# Revit family: LAMP_HANCE SURFACE MEDIUM FLOOD
name_source: partatom
category: Modelos genéricos
revit_build: Autodesk Revit 2015 (Build: 20140606_1530(x64)
units: mm (PartAtom-declared; Revit-internal decimal feet)

## types (16) — shared parameters
CRI = 80
Comentarios de tipo = Availability of tilting between 0º and 90º, rotation between 0º and 355º and change ring color when placed in a project.
Elevación por defecto = 1219 mm
Fabricante = LAMP
Gear = Electronic
Installation instructions = http://www.lamp.es
Insulation class = I
Lamp = LED COB
Last update = 08/08/2018
MacAdam = 3
Manufacturer URL = http://www.lamp.es
Manufacturer country = Spain
Manufacturer name = LAMP
Model explanation = Availability of tilting between 0º and 90º, rotation between 0º and 355º and change ring color when placed in a project.
Power Supply = 220-240V 50-60Hz
Product URL = http://www.lamp.es
Product datasheet = http://www.lamp.es
Protection rating = IP20
Type = COB PHILIPS

## per-type parameters (varying)
- 751LM 3000 BLACK: Altura tija=63 mm  [stored 0.206693 ft]; Anchura tija=23 mm  [stored 0.0754593 ft]; Body height=135 mm  [stored 0.442913 ft]; Descripción=HANCE SUR 1000 WW MFL BK.; Diameter=65 mm  [stored 0.213255 ft]; Efficacy=92 lm/W; Finish=Texturised black; IEE=A+; Initial color=3000 K; Initial intensity=751 lm; LED Lifetime=50.000 L90 B10; Longitud aro=64 mm  [stored 0.209974 ft]; Longitud cuerpo=135 mm  [stored 0.442913 ft]; Luminaire type=Indoor - Spotlight; Material base=LAMP_Aluminio Hance Negro; Material tija=LAMP_Aluminio Hance Negro; Modelo=HS1SF10MF830NBB; Photometric web file=Cuerpo Hance SURFACE MEDIUM FLOOD (tilting) : 751LM 3000 BLACK; Plum=8 W; Power=7 W; Product code=HS1SF10MF830NBB; Profundidad tija=8 mm  [stored 0.0262467 ft]; Radio bse surface=33 mm; Total height=214 mm  [stored 0.7021 ft]; Weight=0.63 kg
- 751LM 3000 WHITE: Altura tija=63 mm  [stored 0.206693 ft]; Anchura tija=23 mm  [stored 0.0754593 ft]; Body height=135 mm  [stored 0.442913 ft]; Descripción=HANCE SUR 1000 WW MFL WH.; Diameter=65 mm  [stored 0.213255 ft]; Efficacy=92 lm/W; Finish=Texturised matt white; IEE=A+; Initial color=3000 K; Initial intensity=751 lm; LED Lifetime=50.000 L90 B10; Longitud aro=64 mm  [stored 0.209974 ft]; Longitud cuerpo=135 mm  [stored 0.442913 ft]; Luminaire type=Indoor - Spotlight; Material base=LAMP_Aluminio Hance Blanco; Material tija=LAMP_Aluminio Hance Blanco; Modelo=HS1SF10MF830NBW; Photometric web file=Cuerpo Hance SURFACE MEDIUM FLOOD (tilting) : 751LM 3000 WHITE; Plum=8 W; Power=7 W; Product code=HS1SF10MF830NBW; Profundidad tija=8 mm  [stored 0.0262467 ft]; Radio bse surface=33 mm; Total height=214 mm  [stored 0.7021 ft]; Weight=0.62 kg
- 794LM 4000 BLACK: Altura tija=63 mm  [stored 0.206693 ft]; Anchura tija=23 mm  [stored 0.0754593 ft]; Body height=135 mm  [stored 0.442913 ft]; Descripción=HANCE SUR 1000 NW MFL BK.; Diameter=65 mm  [stored 0.213255 ft]; Efficacy=97 lm/W; Finish=Texturised black; IEE=A++; Initial color=4000 K; Initial intensity=794 lm; LED Lifetime=50.000 L90 B10; Longitud aro=64 mm  [stored 0.209974 ft]; Longitud cuerpo=135 mm  [stored 0.442913 ft]; Luminaire type=Indoor - Spotlight; Material base=LAMP_Aluminio Hance Negro; Material tija=LAMP_Aluminio Hance Negro; Modelo=HS1SF10MF840NBB; Photometric web file=Cuerpo Hance SURFACE MEDIUM FLOOD (tilting) : 794LM 4000 BLACK; Plum=8 W; Power=7 W; Product code=HS1SF10MF840NBB; Profundidad tija=8 mm  [stored 0.0262467 ft]; Radio bse surface=33 mm; Total height=214 mm  [stored 0.7021 ft]; Weight=0.62 kg
- 794LM 4000 WHITE: Altura tija=63 mm  [stored 0.206693 ft]; Anchura tija=23 mm  [stored 0.0754593 ft]; Body height=135 mm  [stored 0.442913 ft]; Descripción=HANCE SUR 1000 NW MFL WH.; Diameter=65 mm  [stored 0.213255 ft]; Efficacy=97 lm/W; Finish=Texturised matt white; IEE=A++; Initial color=4000 K; Initial intensity=794 lm; LED Lifetime=50.000 L90 B10; Longitud aro=64 mm  [stored 0.209974 ft]; Longitud cuerpo=135 mm  [stored 0.442913 ft]; Luminaire type=Indoor - spotlight; Material base=LAMP_Aluminio Hance Blanco; Material tija=LAMP_Aluminio Hance Blanco; Modelo=HS1SF10MF840NBW; Photometric web file=Cuerpo Hance SURFACE MEDIUM FLOOD (tilting) : 794LM 4000 WHITE; Plum=8 W; Power=7 W; Product code=HS1SF10MF840NBW; Profundidad tija=8 mm  [stored 0.0262467 ft]; Radio bse surface=33 mm; Total height=214 mm  [stored 0.7021 ft]; Weight=0.62 kg
- 1612LM 3000 BLACK: Altura tija=63 mm  [stored 0.206693 ft]; Anchura tija=23 mm  [stored 0.0754593 ft]; Body height=170 mm  [stored 0.557743 ft]; Descripción=HANCE SUR 2000 WW MFL BK.; Diameter=65 mm  [stored 0.213255 ft]; Efficacy=77 lm/W; Finish=Texturised black; IEE=A+; Initial color=3000 K; Initial intensity=1612 lm; LED Lifetime=50.000 L80 B10; Longitud aro=99 mm; Longitud cuerpo=170 mm  [stored 0.557743 ft]; Luminaire type=Indoor - Spotlight; Material base=LAMP_Aluminio Hance Negro; Material tija=LAMP_Aluminio Hance Negro; Modelo=HS1SF20MF830NBB; Photometric web file=Cuerpo Hance SURFACE MEDIUM FLOOD (tilting) : 1612LM 3000 BLACK; Plum=21 W; Power=18 W; Product code=HS1SF20MF830NBB; Profundidad tija=8 mm  [stored 0.0262467 ft]; Radio bse surface=33 mm; Total height=248 mm  [stored 0.813648 ft]; Weight=0.72 kg
- 1612LM 3000 WHITE: Altura tija=63 mm  [stored 0.206693 ft]; Anchura tija=23 mm  [stored 0.0754593 ft]; Body height=170 mm  [stored 0.557743 ft]; Descripción=HANCE SUR 2000 WW MFL WH.; Diameter=65 mm  [stored 0.213255 ft]; Efficacy=77 lm/W; Finish=Texturised matt white; IEE=A+; Initial color=3000 K; Initial intensity=1612 lm; LED Lifetime=50.000 L80 B10; Longitud aro=99 mm; Longitud cuerpo=170 mm  [stored 0.557743 ft]; Luminaire type=Indoor - Spotlight; Material base=LAMP_Aluminio Hance Blanco; Material tija=LAMP_Aluminio Hance Blanco; Modelo=HS1SF20MF830NBW; Photometric web file=Cuerpo Hance SURFACE MEDIUM FLOOD (tilting) : 1612LM 3000 WHITE; Plum=21 W; Power=18 W; Product code=HS1SF20MF830NBW; Profundidad tija=8 mm  [stored 0.0262467 ft]; Radio bse surface=33 mm; Total height=248 mm  [stored 0.813648 ft]; Weight=0.72 kg
- 1703LM 4000 BLACK: Altura tija=63 mm  [stored 0.206693 ft]; Anchura tija=23 mm  [stored 0.0754593 ft]; Body height=170 mm  [stored 0.557743 ft]; Descripción=HANCE SUR 2000 NW MFL BK.; Diameter=65 mm  [stored 0.213255 ft]; Efficacy=81 lm/W; Finish=Texturised black; IEE=A+; Initial color=4000 K; Initial intensity=1703 lm; LED Lifetime=50.000 L80 B10; Longitud aro=99 mm; Longitud cuerpo=170 mm  [stored 0.557743 ft]; Luminaire type=Indoor - Spotlight; Material base=LAMP_Aluminio Hance Negro; Material tija=LAMP_Aluminio Hance Negro; Modelo=HS1SF20MF840NBB; Photometric web file=Cuerpo Hance SURFACE MEDIUM FLOOD (tilting) : 1703LM 4000 BLACK; Plum=21 W; Power=18 W; Product code=HS1SF20MF840NBB; Profundidad tija=8 mm  [stored 0.0262467 ft]; Radio bse surface=33 mm; Total height=248 mm  [stored 0.813648 ft]; Weight=0.72 kg
- 1703LM 4000 WHITE: Altura tija=63 mm  [stored 0.206693 ft]; Anchura tija=23 mm  [stored 0.0754593 ft]; Body height=170 mm  [stored 0.557743 ft]; Descripción=HANCE SUR 2000 NW MFL WH.; Diameter=65 mm  [stored 0.213255 ft]; Efficacy=81 lm/W; Finish=Texturised matt white; IEE=A+; Initial color=4000 K; Initial intensity=1703 lm; LED Lifetime=50.000 L80 B10; Longitud aro=99 mm; Longitud cuerpo=170 mm  [stored 0.557743 ft]; Luminaire type=Indoor - Spotlight; Material base=LAMP_Aluminio Hance Blanco; Material tija=LAMP_Aluminio Hance Blanco; Modelo=HS1SF20MF840NBW; Photometric web file=Cuerpo Hance SURFACE MEDIUM FLOOD (tilting) : 1703LM 4000 WHITE; Plum=21 W; Power=18 W; Product code=HS1SF20MF840NBW; Profundidad tija=8 mm  [stored 0.0262467 ft]; Radio bse surface=33 mm; Total height=248 mm  [stored 0.813648 ft]; Weight=0.72 kg
- 2625LM 3000 BLACK: Altura tija=49 mm  [stored 0.160761 ft]; Anchura tija=28 mm  [stored 0.0918635 ft]; Body height=210 mm  [stored 0.688976 ft]; Descripción=HANCE SUR 3000 WW MFL BK.; Diameter=90 mm  [stored 0.295276 ft]; Efficacy=92 lm/W; Finish=Texturised black; IEE=A+; Initial color=3000 K; Initial intensity=2625 lm; LED Lifetime=50.000 L80 B10; Longitud aro=139 mm; Longitud cuerpo=210 mm  [stored 0.688976 ft]; Luminaire type=Indoor - Spotlight; Material base=LAMP_Aluminio Hance Negro; Material tija=LAMP_Aluminio Hance Negro; Modelo=HS1SF30MF830NBB; Photometric web file=Cuerpo Hance SURFACE MEDIUM FLOOD (tilting) : 2625LM 3000 BLACK; Plum=29 W; Power=26 W; Product code=HS1SF30MF830NBB; Profundidad tija=18 mm  [stored 0.0590551 ft]; Radio bse surface=45 mm  [stored 0.147638 ft]; Total height=290 mm  [stored 0.951444 ft]; Weight=1.34 kg
- 2625LM 3000 WHITE: Altura tija=49 mm  [stored 0.160761 ft]; Anchura tija=28 mm  [stored 0.0918635 ft]; Body height=210 mm  [stored 0.688976 ft]; Descripción=HANCE SUR 3000 WW MFL WH.; Diameter=90 mm  [stored 0.295276 ft]; Efficacy=92 lm/W; Finish=Texturised matt white; IEE=A+; Initial color=3000 K; Initial intensity=2625 lm; LED Lifetime=50.000 L80 B10; Longitud aro=139 mm; Longitud cuerpo=210 mm  [stored 0.688976 ft]; Luminaire type=Indoor - Spotlight; Material base=LAMP_Aluminio Hance Blanco; Material tija=LAMP_Aluminio Hance Blanco; Modelo=HS1SF30MF830NBW; Photometric web file=Cuerpo Hance SURFACE MEDIUM FLOOD (tilting) : 2625LM 3000 WHITE; Plum=29 W; Power=26 W; Product code=HS1SF30MF830NBW; Profundidad tija=18 mm  [stored 0.0590551 ft]; Radio bse surface=45 mm  [stored 0.147638 ft]; Total height=290 mm  [stored 0.951444 ft]; Weight=1.34 kg
- 2744LM 4000 BLACK: Altura tija=49 mm  [stored 0.160761 ft]; Anchura tija=28 mm  [stored 0.0918635 ft]; Body height=210 mm  [stored 0.688976 ft]; Descripción=HANCE SUR 3000 NW MFL BK.; Diameter=90 mm  [stored 0.295276 ft]; Efficacy=96 lm/W; Finish=Texturised black; IEE=A+; Initial color=4000 K; Initial intensity=2744 lm; LED Lifetime=50.000 L80 B10; Longitud aro=139 mm; Longitud cuerpo=210 mm  [stored 0.688976 ft]; Luminaire type=Indoor - Spotlight; Material base=LAMP_Aluminio Hance Negro; Material tija=LAMP_Aluminio Hance Negro; Modelo=HS1SF30MF840NBB; Photometric web file=Cuerpo Hance SURFACE MEDIUM FLOOD (tilting) : 2744LM 4000 BLACK; Plum=29 W; Power=26 W; Product code=HS1SF30MF840NBB; Profundidad tija=18 mm  [stored 0.0590551 ft]; Radio bse surface=45 mm  [stored 0.147638 ft]; Total height=290 mm  [stored 0.951444 ft]; Weight=1.34 kg
- 2744LM 4000 WHITE: Altura tija=49 mm  [stored 0.160761 ft]; Anchura tija=28 mm  [stored 0.0918635 ft]; Body height=210 mm  [stored 0.688976 ft]; Descripción=HANCE SUR 3000 NW MFL WH.; Diameter=90 mm  [stored 0.295276 ft]; Efficacy=96 lm/W; Finish=Texturised matt white; IEE=A+; Initial color=4000 K; Initial intensity=2744 lm; LED Lifetime=50.000 L80 B10; Longitud aro=139 mm; Longitud cuerpo=210 mm  [stored 0.688976 ft]; Luminaire type=Indoor - Spotlight; Material base=LAMP_Aluminio Hance Blanco; Material tija=LAMP_Aluminio Hance Blanco; Modelo=HS1SF30MF840NBW; Photometric web file=Cuerpo Hance SURFACE MEDIUM FLOOD (tilting) : 2744LM 4000 WHITE; Plum=29 W; Power=26 W; Product code=HS1SF30MF840NBW; Profundidad tija=18 mm  [stored 0.0590551 ft]; Radio bse surface=45 mm  [stored 0.147638 ft]; Total height=290 mm  [stored 0.951444 ft]; Weight=1.34 kg
- 3387LM 3000 BLACK: Altura tija=49 mm  [stored 0.160761 ft]; Anchura tija=28 mm  [stored 0.0918635 ft]; Body height=210 mm  [stored 0.688976 ft]; Descripción=HANCE SUR 4000 WW MFL BK.; Diameter=90 mm  [stored 0.295276 ft]; Efficacy=86 lm/W; Finish=Texturised black; IEE=A+; Initial color=3000 K; Initial intensity=3387 lm; LED Lifetime=50.000 L80 B10; Longitud aro=139 mm; Longitud cuerpo=210 mm  [stored 0.688976 ft]; Luminaire type=Indoor - Spotlight; Material base=LAMP_Aluminio Hance Negro; Material tija=LAMP_Aluminio Hance Negro; Modelo=HS1SF40MF830NBB; Photometric web file=Cuerpo Hance SURFACE MEDIUM FLOOD (tilting) : 3387LM 3000 BLACK; Plum=40 W; Power=35 W; Product code=HS1SF40MF830NBB; Profundidad tija=18 mm  [stored 0.0590551 ft]; Radio bse surface=45 mm  [stored 0.147638 ft]; Total height=290 mm  [stored 0.951444 ft]; Weight=1.34 kg
- 3387LM 3000 WHITE: Altura tija=49 mm  [stored 0.160761 ft]; Anchura tija=28 mm  [stored 0.0918635 ft]; Body height=210 mm  [stored 0.688976 ft]; Descripción=HANCE SUR 4000 WW MFL WH.; Diameter=90 mm  [stored 0.295276 ft]; Efficacy=86 lm/W; Finish=Texturised matt white; IEE=A+; Initial color=3000 K; Initial intensity=3387 lm; LED Lifetime=50.000 L80 B10; Longitud aro=139 mm; Longitud cuerpo=210 mm  [stored 0.688976 ft]; Luminaire type=Indoor - Spotlight; Material base=LAMP_Aluminio Hance Blanco; Material tija=LAMP_Aluminio Hance Blanco; Modelo=HS1SF40MF830NBW; Photometric web file=Cuerpo Hance SURFACE MEDIUM FLOOD (tilting) : 3387LM 3000 WHITE; Plum=40 W; Power=35 W; Product code=HS1SF40MF830NBW; Profundidad tija=18 mm  [stored 0.0590551 ft]; Radio bse surface=45 mm  [stored 0.147638 ft]; Total height=290 mm  [stored 0.951444 ft]; Weight=1.34 kg
- 3527LM 4000 BLACK: Altura tija=49 mm  [stored 0.160761 ft]; Anchura tija=28 mm  [stored 0.0918635 ft]; Body height=210 mm  [stored 0.688976 ft]; Descripción=HANCE SUR 4000 NW MFL BK.; Diameter=90 mm  [stored 0.295276 ft]; Efficacy=89 lm/W; Finish=Texturised black; IEE=A+; Initial color=4000 K; Initial intensity=3527 lm; LED Lifetime=50.000 L80 B10; Longitud aro=139 mm; Longitud cuerpo=210 mm  [stored 0.688976 ft]; Luminaire type=Indoor - Spotlight; Material base=LAMP_Aluminio Hance Negro; Material tija=LAMP_Aluminio Hance Negro; Modelo=HS1SF40MF840NBB; Photometric web file=Cuerpo Hance SURFACE MEDIUM FLOOD (tilting) : 3527LM 4000 BLACK; Plum=40 W; Power=35 W; Product code=HS1SF40MF840NBB; Profundidad tija=18 mm  [stored 0.0590551 ft]; Radio bse surface=45 mm  [stored 0.147638 ft]; Total height=290 mm  [stored 0.951444 ft]; Weight=1.34 kg
- 3527LM 4000 WHITE: Altura tija=49 mm  [stored 0.160761 ft]; Anchura tija=28 mm  [stored 0.0918635 ft]; Body height=210 mm  [stored 0.688976 ft]; Descripción=HANCE SUR 4000 NW MFL WH.; Diameter=90 mm  [stored 0.295276 ft]; Efficacy=89 lm/W; Finish=Texturised matt white; IEE=A+; Initial color=4000 K; Initial intensity=3527 lm; LED Lifetime=50.000 L80 B10; Longitud aro=139 mm; Longitud cuerpo=210 mm  [stored 0.688976 ft]; Luminaire type=Indoor - Spotlight; Material base=LAMP_Aluminio Hance Blanco; Material tija=LAMP_Aluminio Hance Blanco; Modelo=HS1SF40MF840NBW; Photometric web file=Cuerpo Hance SURFACE MEDIUM FLOOD (tilting) : 3527LM 4000 WHITE; Plum=40 W; Power=35 W; Product code=HS1SF40MF840NBW; Profundidad tija=18 mm  [stored 0.0590551 ft]; Radio bse surface=45 mm  [stored 0.147638 ft]; Total height=290 mm  [stored 0.951444 ft]; Weight=1.34 kg

note: [stored X ft] marks values corroborated as IEEE doubles in the binary element streams (Revit-internal decimal feet)
